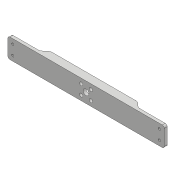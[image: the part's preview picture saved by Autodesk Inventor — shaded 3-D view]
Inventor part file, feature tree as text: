
AUTODESK INVENTOR PART (.ipt)
format: ipt  version: 2018 (Build 220112000, 112)  size: 158,208 bytes
history: native  units: mm
features: sketch x4, extrude x3, fillet x3, hole x2, projected_geometry x2, chamfer x1, mirror x1
ambient origin geometry x8: Origin, YZ Plane, XZ Plane, XY Plane, X Axis, Y Axis, Z Axis, Center Point
bodies: Solid1 (feature_tree)
feature tree (16):
  extrude  "Extrusion1"  Depth=160.0mm
  sketch  "Sketch2"  dims[d6=3.0mm d7=0.0mm d8=14.0mm]
  hole  "Hole1"  [1 undecoded]
  extrude  "Extrusion2"  Depth=9.899495mm
  hole  "Hole2"  [1 undecoded]
  fillet  "Fillet1"  Radius=2.0mm
  extrude  "Extrusion3"  Depth=10.0mm
  chamfer  "Chamfer1"  Distance=150.0mm
  fillet  "Fillet2"  Radius=2.0mm
  fillet  "Fillet3"  Radius=100.0mm
  mirror  "Mirror1"
  sketch  "Sketch1"  dims[d0=20.0mm d1=160.0mm]
  projected_geometry  "Projected Loop1"
  sketch  "Sketch3"  dims[d9=9.899495mm d10=9.899495mm]
  sketch  "Sketch4"  dims[d12=3.4mm d13=6.0mm d14=6.3mm d15=2.0mm d16=90.0deg d17=8.0mm d18=20.594885mm d19=6.0mm d20=2.0mm d21=0.0mm d22=10.0mm d23=150.0mm d24=2.459mm d25=6.0mm d26=6.3mm d27=2.0mm d28=90.0deg d29=8.8mm d30=20.594885mm d31=2.0mm d32=100.0mm d33=5.0mm d34=1.5mm d35=0.0mm d36=5.0mm d37=2.0mm d38=45.0deg d39=5.0mm d40=1.0mm]
  projected_geometry  "Projected Loop2"
note: 2 required parameter values undecoded (feature->parameter linkage not recoverable at this tier; creation-order binding heuristic only, values carry confidence <= 0.55)
